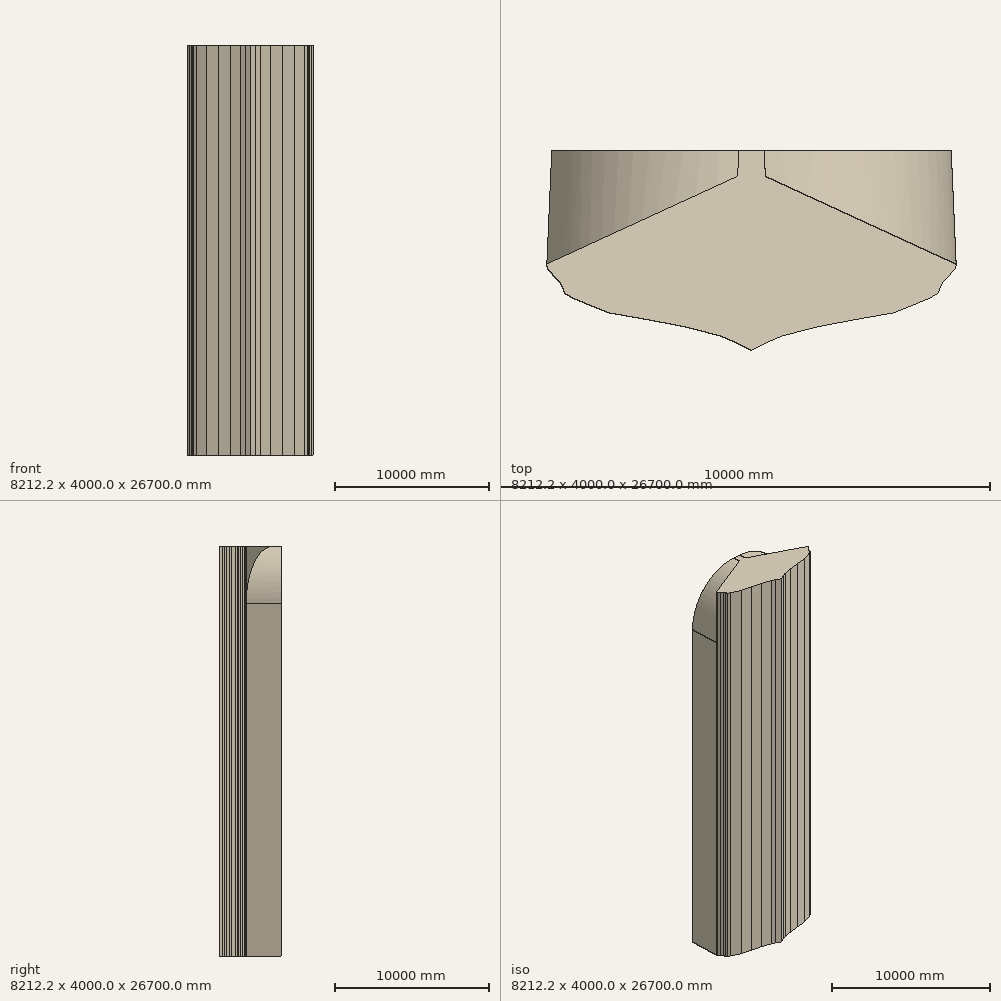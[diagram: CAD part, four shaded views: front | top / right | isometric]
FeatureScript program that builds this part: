
annotation { "Feature Type Name" : "Feature", "Feature Type Description" : "" }
export const myFeature = defineFeature(function(context is Context, id is Id, definition is map)
    precondition{}
    {
        {
            var Q0;
            Q0=qCreatedBy(makeId("Top.planeOp"),FACE);
            var sketch = newSketch(context, id + "F0", { "sketchPlane" : qUnion([Q0])});
            skLineSegment(sketch, "E0", {"start": v(0, 0) * mm, "end": v(0, 4000) * mm});
            skLineSegment(sketch, "E1", {"start": v(0, 4000) * mm, "end": v(-4000, 4000) * mm});
            skLineSegment(sketch, "E2", {"start": v(-4000, 4000) * mm, "end": v(-4099.38, 1725.3) * mm});
            skLineSegment(sketch, "E3", {"start": v(-4099.38, 1725.3) * mm, "end": v(-4106.1, 1722.2) * mm});
            skLineSegment(sketch, "E4", {"start": v(-4106.1, 1722.2) * mm, "end": v(-4102.93, 1698.48) * mm});
            skLineSegment(sketch, "E5", {"start": v(-4102.93, 1698.48) * mm, "end": v(-4085.33, 1639.44) * mm});
            skLineSegment(sketch, "E6", {"start": v(-4085.33, 1639.44) * mm, "end": v(-3978.97, 1508.45) * mm});
            skLineSegment(sketch, "E7", {"start": v(-3978.97, 1508.45) * mm, "end": v(-3845.66, 1375.14) * mm});
            skLineSegment(sketch, "E8", {"start": v(-3845.66, 1375.14) * mm, "end": v(-3781.23, 1250.72) * mm});
            skLineSegment(sketch, "E9", {"start": v(-3781.23, 1250.72) * mm, "end": v(-3739.01, 1132.96) * mm});
            skLineSegment(sketch, "E10", {"start": v(-3739.01, 1132.96) * mm, "end": v(-3535.4, 1026.07) * mm});
            skLineSegment(sketch, "E11", {"start": v(-3535.4, 1026.07) * mm, "end": v(-2867.43, 752.8) * mm});
            skLineSegment(sketch, "E12", {"start": v(-2867.43, 752.8) * mm, "end": v(-2057.77, 611.11) * mm});
            skLineSegment(sketch, "E13", {"start": v(-2057.77, 611.11) * mm, "end": v(-1318.95, 469.42) * mm});
            skLineSegment(sketch, "E14", {"start": v(-1318.95, 469.42) * mm, "end": v(-620.62, 287.25) * mm});
            skLineSegment(sketch, "E15", {"start": v(-620.62, 287.25) * mm, "end": v(-357.48, 175.92) * mm});
            skLineSegment(sketch, "E16", {"start": v(-357.48, 175.92) * mm, "end": v(0, 0) * mm});
            skLineSegment(sketch, "E17.MirrorCS", {"start": v(357.48, 175.92) * mm, "end": v(0, 0) * mm});
            skLineSegment(sketch, "E18.MirrorCS", {"start": v(620.62, 287.25) * mm, "end": v(357.48, 175.92) * mm});
            skLineSegment(sketch, "E19.MirrorCS", {"start": v(1318.95, 469.42) * mm, "end": v(620.62, 287.25) * mm});
            skLineSegment(sketch, "E20.MirrorCS", {"start": v(2057.77, 611.11) * mm, "end": v(1318.95, 469.42) * mm});
            skLineSegment(sketch, "E21.MirrorCS", {"start": v(2867.43, 752.8) * mm, "end": v(2057.77, 611.11) * mm});
            skLineSegment(sketch, "E22.MirrorCS", {"start": v(3535.4, 1026.07) * mm, "end": v(2867.43, 752.8) * mm});
            skLineSegment(sketch, "E23.MirrorCS", {"start": v(3781.23, 1250.72) * mm, "end": v(3739.01, 1132.96) * mm});
            skLineSegment(sketch, "E24.MirrorCS", {"start": v(3845.66, 1375.14) * mm, "end": v(3781.23, 1250.72) * mm});
            skLineSegment(sketch, "E25.MirrorCS", {"start": v(3978.97, 1508.45) * mm, "end": v(3845.66, 1375.14) * mm});
            skLineSegment(sketch, "E26.MirrorCS", {"start": v(4085.33, 1639.44) * mm, "end": v(3978.97, 1508.45) * mm});
            skLineSegment(sketch, "E27.MirrorCS", {"start": v(4102.93, 1698.48) * mm, "end": v(4085.33, 1639.44) * mm});
            skLineSegment(sketch, "E28.MirrorCS", {"start": v(4106.1, 1722.2) * mm, "end": v(4102.93, 1698.48) * mm});
            skLineSegment(sketch, "E29.MirrorCS", {"start": v(3739.01, 1132.96) * mm, "end": v(3535.4, 1026.07) * mm});
            skLineSegment(sketch, "E30.MirrorCS", {"start": v(4099.38, 1725.3) * mm, "end": v(4106.1, 1722.2) * mm});
            skLineSegment(sketch, "E31.MirrorCS", {"start": v(4000, 4000) * mm, "end": v(4099.38, 1725.3) * mm});
            skLineSegment(sketch, "E32.MirrorCS", {"start": v(0, 4000) * mm, "end": v(4000, 4000) * mm});
            skSolve(sketch);
        }
        {
            var Q0;
            Q0=makeQuery(id+"F0.imprint","IMPRINT",FACE,{"disambiguationData":[TD([[makeQuery(id+"F0.imprint","IMPRINT",EDGE,{"derivedFrom":sQuery(id+"F0.wireOp",EDGE,"E0")}),1.0]])]});
            var Q1;
            Q1=makeQuery(id+"F0.imprint","IMPRINT",FACE,{"disambiguationData":[TD([[makeQuery(id+"F0.imprint","IMPRINT",EDGE,{"derivedFrom":sQuery(id+"F0.wireOp",EDGE,"E0")}),-1.0]])]});
            extrude(context, id + "F1", {"entities" : qUnion([Q0, Q1]), "depth" : 26700 * mm, "offsetDistance" : 25 * mm});
        }
        {
            var Q0;
            Q0=makeQuery(id+"F1.opExtrude","CAP_EDGE",EDGE,{"disambiguationData":[OSD([sQuery(id+"F0.wireOp",EDGE,"E2")])],"isStart":false});
            var Q1;
            Q1=makeQuery(id+"F1.opExtrude","CAP_EDGE",EDGE,{"disambiguationData":[OSD([sQuery(id+"F0.wireOp",EDGE,"E31.MirrorCS")])],"isStart":false});
            fillet(context, id + "F2", {"entities" : qUnion([Q0, Q1]), "radius" : 3742.03 * mm, "tangentPropagation" : true, "allowEdgeOverflow" : false});
        }
    });
